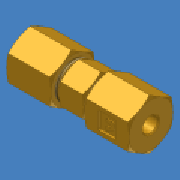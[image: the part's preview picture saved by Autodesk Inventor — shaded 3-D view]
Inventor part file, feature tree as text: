
AUTODESK INVENTOR PART (.ipt)
format: ipt  version: 2018 (Build 220112000, 112)  size: 303,104 bytes
history: native  units: in
note: dims shown in document units (in); Inventor stores cm internally (conversion verified against a paired STEP export)
features: other x2, sketch x1, imported_body x1
ambient origin geometry x8: Origin, YZ Plane, XZ Plane, XY Plane, X Axis, Y Axis, Z Axis, Center Point
bodies: Solid1 (feature_tree)
feature tree (4):
  other  "Table"
  other  "Union 62C.ipt"
  sketch  "Sketch1"
  imported_body  "DerivedBody::Union 62C.ipt"
